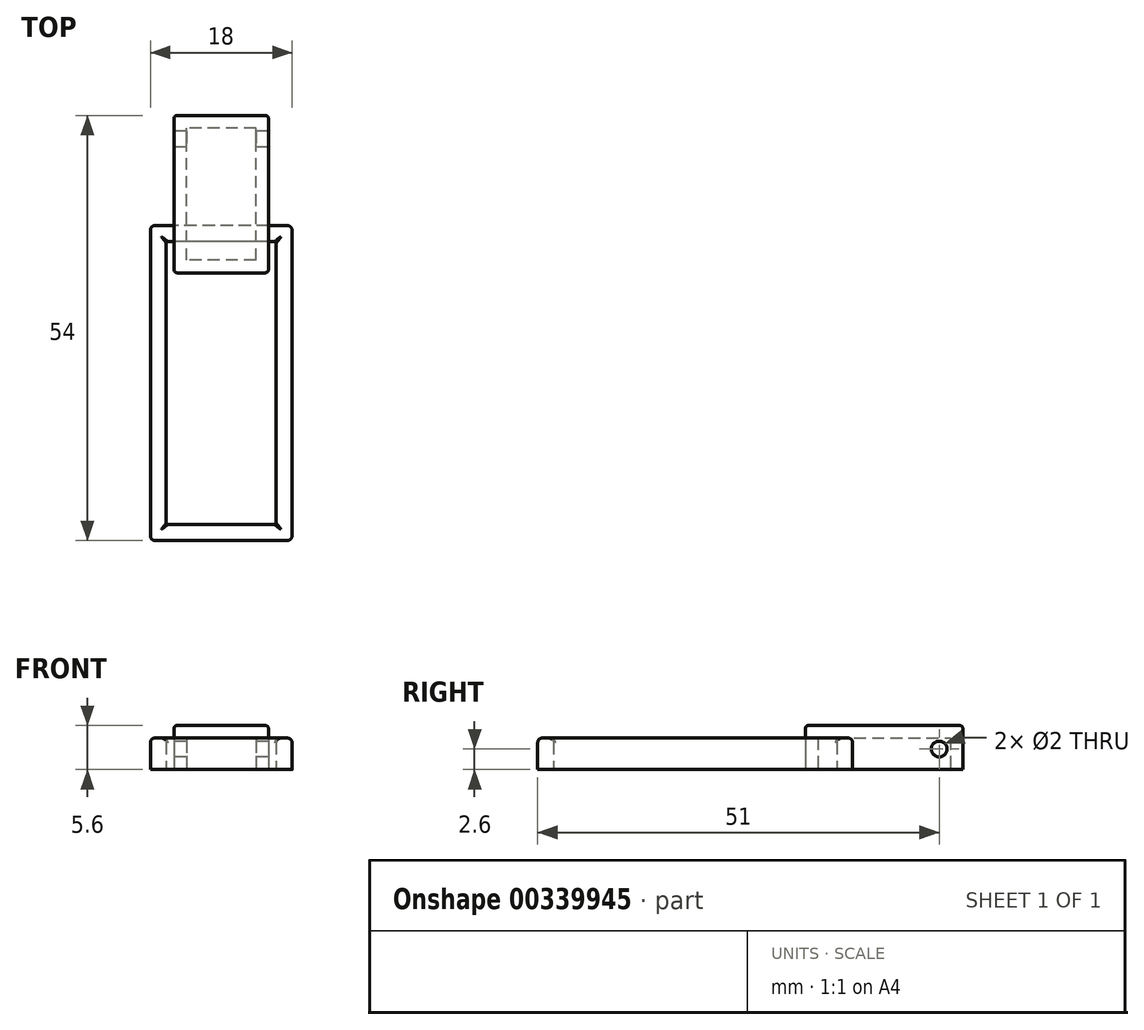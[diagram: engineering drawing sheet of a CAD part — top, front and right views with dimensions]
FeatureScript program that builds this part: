
annotation { "Feature Type Name" : "Feature", "Feature Type Description" : "" }
export const myFeature = defineFeature(function(context is Context, id is Id, definition is map)
    precondition{}
    {
        {
            var Q0;
            Q0=qCreatedBy(makeId("Top.planeOp"),FACE);
            var sketch = newSketch(context, id + "F0", { "sketchPlane" : qUnion([Q0])});
            skLineSegment(sketch, "E0.bottom", {"start": v(6, -10) * mm, "end": v(-6, -10) * mm});
            skLineSegment(sketch, "E0.top", {"start": v(6, 10) * mm, "end": v(-6, 10) * mm});
            skLineSegment(sketch, "E0.left", {"start": v(6, -10) * mm, "end": v(6, 10) * mm});
            skLineSegment(sketch, "E0.right", {"start": v(-6, -10) * mm, "end": v(-6, 10) * mm});
            skPoint(sketch, "E0.middle", {"position": v(0, 0) * mm});
            skSolve(sketch);
        }
        {
            var Q0;
            Q0=qSketchRegion(id+"F0",true);
            extrude(context, id + "F1", {"entities" : qUnion([Q0]), "depth" : 5.6 * mm});
        }
        {
            var Q0;
            Q0=makeQuery(id+"F1.opExtrude","CAP_FACE",FACE,{"disambiguationData":[OSD([sQuery(id+"F0.wireOp",EDGE,"E0.bottom"),sQuery(id+"F0.wireOp",EDGE,"E0.top"),sQuery(id+"F0.wireOp",EDGE,"E0.left"),sQuery(id+"F0.wireOp",EDGE,"E0.right")])],"isStart":true});
            shell(context, id + "F2", {"entities" : qUnion([Q0]), "thickness" : 1.6 * mm});
        }
        {
            var Q0;
            Q0=qCreatedBy(makeId("Top.planeOp"),FACE);
            var sketch = newSketch(context, id + "F3", { "sketchPlane" : qUnion([Q0])});
            skLineSegment(sketch, "E1.bottom", {"start": v(9, -4) * mm, "end": v(-9, -4) * mm});
            skLineSegment(sketch, "E1.top", {"start": v(9, -44) * mm, "end": v(-9, -44) * mm});
            skLineSegment(sketch, "E1.left", {"start": v(9, -4) * mm, "end": v(9, -44) * mm});
            skLineSegment(sketch, "E1.right", {"start": v(-9, -4) * mm, "end": v(-9, -44) * mm});
            skPoint(sketch, "E1.middle", {"position": v(0, -24) * mm});
            skLineSegment(sketch, "E2.0", {"start": v(7, -6) * mm, "end": v(-7, -6) * mm});
            skLineSegment(sketch, "E2.1", {"start": v(7, -6) * mm, "end": v(7, -42) * mm});
            skLineSegment(sketch, "E2.2", {"start": v(7, -42) * mm, "end": v(-7, -42) * mm});
            skLineSegment(sketch, "E2.3", {"start": v(-7, -6) * mm, "end": v(-7, -42) * mm});
            skLineSegment(sketch, "E3", {"start": v(0, 0) * mm, "end": v(0, -6) * mm, "construction": true});
            skSolve(sketch);
        }
        {
            var Q0;
            Q0=qSketchRegion(id+"F3",true);
            extrude(context, id + "F4", {"entities" : qUnion([Q0]), "depth" : 4 * mm, "hasSecondDirection" : true, "secondDirectionOppositeDirection" : false, "secondDirectionDepth" : 0 * mm});
        }
        {
            var Q0;
            Q0=makeQuery(id+"F1.opExtrude","CAP_FACE",FACE,{"disambiguationData":[OSD([sQuery(id+"F0.wireOp",EDGE,"E0.bottom"),sQuery(id+"F0.wireOp",EDGE,"E0.top"),sQuery(id+"F0.wireOp",EDGE,"E0.left"),sQuery(id+"F0.wireOp",EDGE,"E0.right")])],"isStart":false});
            var Q1;
            Q1=makeQuery(id+"F1.opExtrude","SWEPT_EDGE",EDGE,{"disambiguationData":[OSD([sQuery(id+"F0.wireOp",EDGE,"E0.top"),sQuery(id+"F0.wireOp",EDGE,"E0.right")])]});
            var Q2;
            Q2=makeQuery(id+"F1.opExtrude","SWEPT_EDGE",EDGE,{"disambiguationData":[OSD([sQuery(id+"F0.wireOp",EDGE,"E0.bottom"),sQuery(id+"F0.wireOp",EDGE,"E0.right")])]});
            var Q3;
            Q3=makeQuery(id+"F1.opExtrude","SWEPT_EDGE",EDGE,{"disambiguationData":[OSD([sQuery(id+"F0.wireOp",EDGE,"E0.bottom"),sQuery(id+"F0.wireOp",EDGE,"E0.left")])]});
            var Q4;
            Q4=makeQuery(id+"F1.opExtrude","SWEPT_EDGE",EDGE,{"disambiguationData":[OSD([sQuery(id+"F0.wireOp",EDGE,"E0.top"),sQuery(id+"F0.wireOp",EDGE,"E0.left")])]});
            fillet(context, id + "F5", {"entities" : qUnion([Q0, Q1, Q2, Q3, Q4]), "radius" : 0.4 * mm, "tangentPropagation" : true, "allowEdgeOverflow" : false});
        }
        {
            var Q0;
            Q0=makeQuery(id+"F4.opExtrude","CAP_FACE",FACE,{"disambiguationData":[OSD([sQuery(id+"F3.wireOp",EDGE,"E1.bottom"),sQuery(id+"F3.wireOp",EDGE,"E1.top"),sQuery(id+"F3.wireOp",EDGE,"E1.left"),sQuery(id+"F3.wireOp",EDGE,"E1.right"),sQuery(id+"F3.wireOp",EDGE,"E2.0"),sQuery(id+"F3.wireOp",EDGE,"E2.1"),sQuery(id+"F3.wireOp",EDGE,"E2.2"),sQuery(id+"F3.wireOp",EDGE,"E2.3")])],"isStart":false});
            var Q1;
            Q1=makeQuery(id+"F4.opExtrude","SWEPT_EDGE",EDGE,{"disambiguationData":[OSD([sQuery(id+"F3.wireOp",EDGE,"E1.bottom"),sQuery(id+"F3.wireOp",EDGE,"E1.right")])]});
            var Q2;
            Q2=makeQuery(id+"F4.opExtrude","SWEPT_EDGE",EDGE,{"disambiguationData":[OSD([sQuery(id+"F3.wireOp",EDGE,"E1.bottom"),sQuery(id+"F3.wireOp",EDGE,"E1.left")])]});
            var Q3;
            Q3=makeQuery(id+"F4.opExtrude","SWEPT_EDGE",EDGE,{"disambiguationData":[OSD([sQuery(id+"F3.wireOp",EDGE,"E1.top"),sQuery(id+"F3.wireOp",EDGE,"E1.left")])]});
            var Q4;
            Q4=makeQuery(id+"F4.opExtrude","SWEPT_EDGE",EDGE,{"disambiguationData":[OSD([sQuery(id+"F3.wireOp",EDGE,"E1.top"),sQuery(id+"F3.wireOp",EDGE,"E1.right")])]});
            fillet(context, id + "F6", {"entities" : qUnion([Q0, Q1, Q2, Q3, Q4]), "radius" : 0.6 * mm, "tangentPropagation" : true, "allowEdgeOverflow" : false});
        }
        {
            var Q0;
            Q0=makeQuery(id+"F4.opExtrude","SWEPT_EDGE",EDGE,{"disambiguationData":[OSD([sQuery(id+"F3.wireOp",EDGE,"E2.0"),sQuery(id+"F3.wireOp",EDGE,"E2.3")])]});
            var Q1;
            Q1=makeQuery(id+"F4.opExtrude","SWEPT_EDGE",EDGE,{"disambiguationData":[OSD([sQuery(id+"F3.wireOp",EDGE,"E2.0"),sQuery(id+"F3.wireOp",EDGE,"E2.1")])]});
            var Q2;
            Q2=makeQuery(id+"F4.opExtrude","SWEPT_EDGE",EDGE,{"disambiguationData":[OSD([sQuery(id+"F3.wireOp",EDGE,"E2.2"),sQuery(id+"F3.wireOp",EDGE,"E2.3")])]});
            var Q3;
            Q3=makeQuery(id+"F4.opExtrude","SWEPT_EDGE",EDGE,{"disambiguationData":[OSD([sQuery(id+"F3.wireOp",EDGE,"E2.1"),sQuery(id+"F3.wireOp",EDGE,"E2.2")])]});
            fillet(context, id + "F7", {"entities" : qUnion([Q0, Q1, Q2, Q3]), "radius" : 0.2 * mm, "tangentPropagation" : true, "allowEdgeOverflow" : false});
        }
        {
            var Q0;
            Q0=makeQuery(id+"F1.opExtrude","SWEPT_FACE",FACE,{"disambiguationData":[OSD([sQuery(id+"F0.wireOp",EDGE,"E0.right")])]});
            var sketch = newSketch(context, id + "F8", { "sketchPlane" : qUnion([Q0])});
            skCircle(sketch, "E4", {"center": v(-7, 2.6) * mm, "radius": 1 * mm});
            skPoint(sketch, "E4.centerSnap0", {"position": v(-9.6, 2.6) * mm});
            skSolve(sketch);
        }
        {
            var Q0;
            Q0=qSketchRegion(id+"F8",true);
            extrude(context, id + "F9", {"entities" : qUnion([Q0]), "operationType" : NewBodyOperationType.REMOVE, "oppositeDirection" : true, "depth" : 25 * mm});
        }
    });
